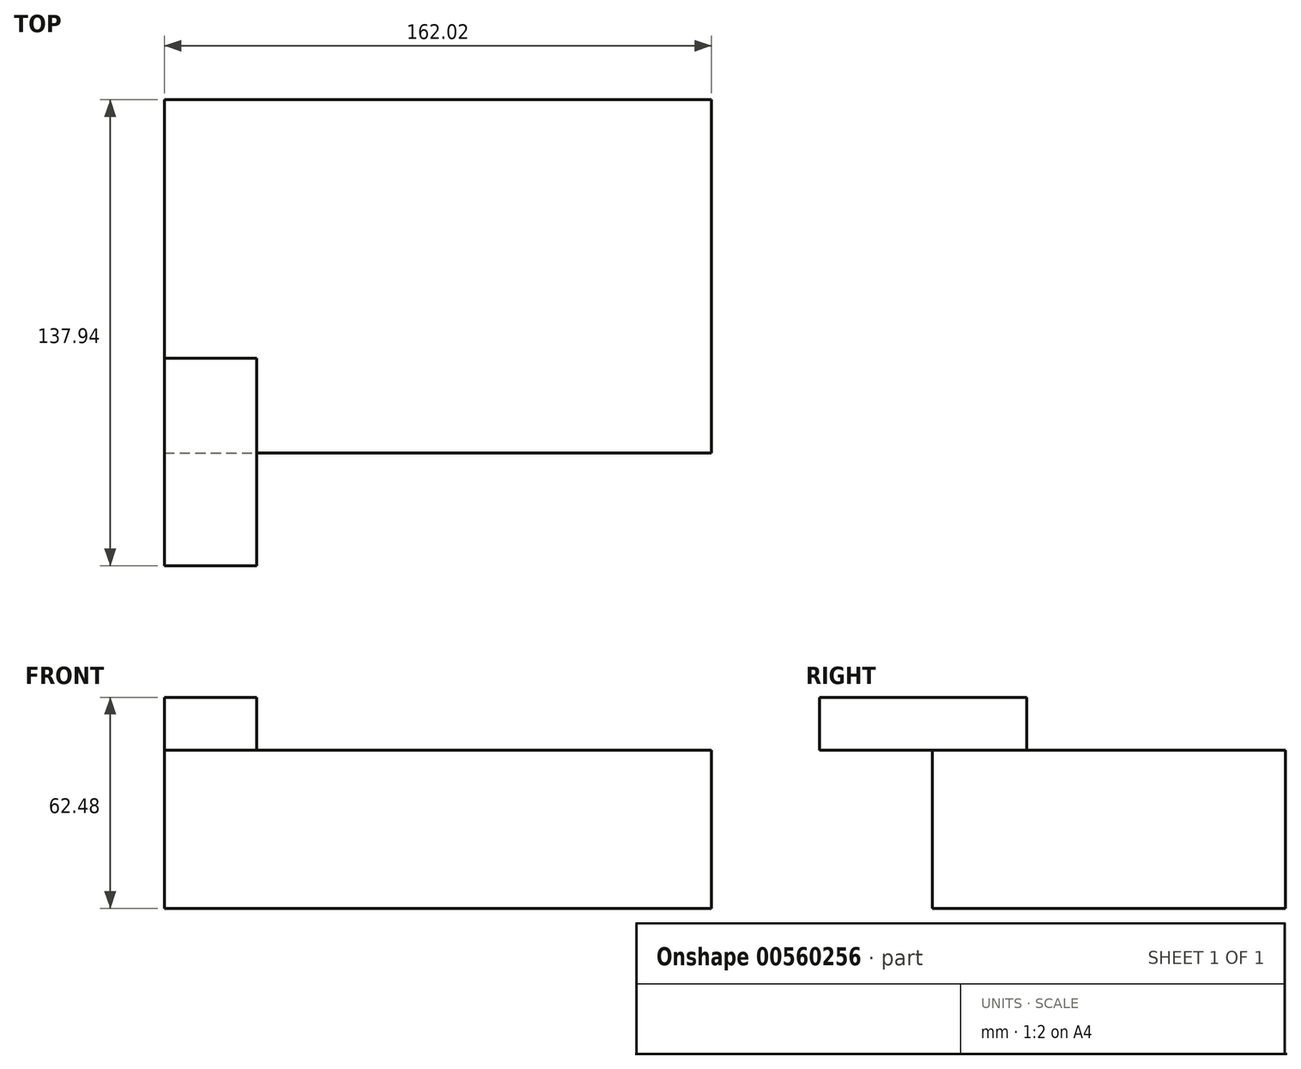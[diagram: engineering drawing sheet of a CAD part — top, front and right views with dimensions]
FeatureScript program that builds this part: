
annotation { "Feature Type Name" : "Feature", "Feature Type Description" : "" }
export const myFeature = defineFeature(function(context is Context, id is Id, definition is map)
    precondition{}
    {
        {
            var Q0;
            Q0=qCreatedBy(makeId("Front.planeOp"),FACE);
            var sketch = newSketch(context, id + "F0", { "sketchPlane" : qUnion([Q0])});
            skLineSegment(sketch, "E0.bottom", {"start": v(52.77, 46.83) * mm, "end": v(0, 46.83) * mm});
            skLineSegment(sketch, "E0.top", {"start": v(52.77, 0) * mm, "end": v(0, 0) * mm});
            skLineSegment(sketch, "E0.left", {"start": v(52.77, 46.83) * mm, "end": v(52.77, 0) * mm});
            skLineSegment(sketch, "E0.right", {"start": v(0, 46.83) * mm, "end": v(0, 0) * mm});
            skSolve(sketch);
        }
        {
            var Q0;
            Q0=makeQuery(id+"F0.imprint","IMPRINT",FACE,{"disambiguationData":[TD([[makeQuery(id+"F0.imprint","IMPRINT",EDGE,{"derivedFrom":sQuery(id+"F0.wireOp",EDGE,"E0.bottom")}),1.0]])]});
            extrude(context, id + "F1", {"entities" : qUnion([Q0]), "depth" : 45.02 * mm, "offsetDistance" : 25.4 * mm});
        }
        {
            var Q0;
            Q0=qCreatedBy(makeId("Right.planeOp"),FACE);
            var sketch = newSketch(context, id + "F2", { "sketchPlane" : qUnion([Q0])});
            skLineSegment(sketch, "E1.bottom", {"start": v(-17.01, 46.8) * mm, "end": v(-78.38, 46.8) * mm});
            skLineSegment(sketch, "E1.top", {"start": v(-17.01, 62.48) * mm, "end": v(-78.38, 62.48) * mm});
            skLineSegment(sketch, "E1.left", {"start": v(-17.01, 46.8) * mm, "end": v(-17.01, 62.48) * mm});
            skLineSegment(sketch, "E1.right", {"start": v(-78.38, 46.8) * mm, "end": v(-78.38, 62.48) * mm});
            skSolve(sketch);
        }
        {
            var Q0;
            Q0=qSketchRegion(id+"F2",true);
            extrude(context, id + "F3", {"entities" : qUnion([Q0]), "operationType" : NewBodyOperationType.ADD, "depth" : 27.4 * mm, "offsetDistance" : 25.4 * mm});
        }
        {
            var Q0;
            Q0=qSketchRegion(id+"FjQz50eirqj7Hvc_1",true);
            var Q1;
            Q1=makeQuery(id+"F1.opExtrude","SWEPT_FACE",FACE,{"disambiguationData":[OSD([sQuery(id+"F0.wireOp",EDGE,"E0.left")])]});
            extrude(context, id + "F4", {"entities" : qUnion([Q0, Q1]), "operationType" : NewBodyOperationType.ADD, "depth" : 109.25 * mm, "offsetDistance" : 25.4 * mm});
        }
        {
            var Q0;
            {var subQ0=sQuery(id+"F0.wireOp",EDGE,"E0.left");Q0=makeQuery(id+"F4.boolean.opBoolean","MERGE",FACE,{"derivedFrom":[makeQuery(id+"F1.opExtrude","CAP_FACE",FACE,{"disambiguationData":[OSD([sQuery(id+"F0.wireOp",EDGE,"E0.bottom"),sQuery(id+"F0.wireOp",EDGE,"E0.top"),subQ0,sQuery(id+"F0.wireOp",EDGE,"E0.right")])],"isStart":true}),makeQuery(id+"F4.opExtrude","SWEPT_FACE",FACE,{"disambiguationData":[OSD([subQ0]),TDD([makeQuery(id+"F1.opExtrude","CAP_EDGE",EDGE,{"disambiguationData":[OSD([subQ0])],"isStart":true})])]})]});}
            extrude(context, id + "F5", {"entities" : qUnion([Q0]), "operationType" : NewBodyOperationType.ADD, "depth" : 59.56 * mm, "offsetDistance" : 25.4 * mm});
        }
    });
